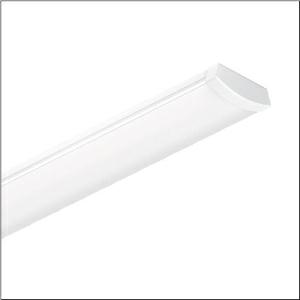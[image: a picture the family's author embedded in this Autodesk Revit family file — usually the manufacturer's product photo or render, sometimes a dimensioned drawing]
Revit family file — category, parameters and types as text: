
# Revit family: siluette_r__21_51ln12mnm70a_66ce
name_source: partatom
category: Lighting Fixtures
units: mm (PartAtom-declared; Revit-internal decimal feet)

## family parameters
Cut with Voids When Loaded = No
Host = Face
Light Source = No
Part Type = Normal
Room Calculation Point = No
Round Connector Dimension = Use Diameter
Shared = No

## types (1)
- --- (1 x LED, 4320 lm, 28.8 W, 5000K)
    Apparent Load = 29 VA
    CIE Flux Codes = 43 73 92 94 100
    Color Rendering = 80
    Color Temperature = 5000K
    Default Elevation = 1800 mm
    Description = Siluette® 21, office luminaire, primary optical cover: enclosure, of PC, frosted, light emission: direct distribution, primary light characteristic: symmetric, installation type: suspended mounting, surface-mounted, LED, rated luminous flux: 7.150lm, luminous efficacy: 140lm/W, light colour: 830/840/850, colour temperature: 3000/4000/5000K, with terminal, 3-pole, mains connection: 220..240V, AC, 50/60Hz, rated input power: 50W, housing, of sheet steel, white, length: 1.500mm, width: 152mm, height: 53mm, end cap, of PMMA, white, protection rating (complete): IP44, insulation class (complete): insulation class I (protective earthing), certification: CE, UKCA, protection symbol: D, permissible operating ambient temperature: -20..+40°C, contact your sales advisor before using the luminaires in applications with unclear chemical exposure, large temperature fluctuations or condensation-forming humidity, corresponds to IFS (International Featured Standards) requirements for safety and quality in the food industry, packaging unit: 1 piece
    Height = 52 mm  [stored 0.170604 ft]
    Lamp = 1 x LED
    Lamp Light Flux = 4320 lm
    Lamp Power = 28.8 W
    Lamp count = 1
    Length = 1485 mm
    Luminous efficacy = 150 lm/W
    Manufacturer = Siteco
    ModVariant = No
    Model = 51LN12MNM70A
    Mounting Place = Ceiling
    Mounting Type = Pendant
    Number of Poles = 1
    OnlyDefault = Yes
    Power Factor = 1
    Product Name = Siluette® 21
    Product group = office luminaire | ceiling pendant
    ProductGroupID = 902
    Protection Class = Protection class I
    Protection Degree = IP 44
    RLX_Detail_Level = 1
    RLX_Emergency_Light_Flux = 0 lm
    RLX_Emergency_Type = 0
    RLX_Emergency_Type_DB = No
    RlxData = <blob elided: 20193 chars, md5=e2df0758>
    Socket = socket
    Standby Power = 0 W
    System Light Flux = 4320 lm
    System Power = 29 W
    Type Comments = individual setting: colour temperature 5000K, luminous flux: 61 % | (OFF | OFF | ON) | 200 mA
    Type Image = l_1296910.jpg
    URL = http://relux.com
    VarID = @adj_019193
    Voltage = 0 V
    Weight = 0.00 kg
    Width = 152 mm

note: [stored X ft] marks values corroborated as IEEE doubles in the binary element streams (Revit-internal decimal feet)

## geometry (parser evidence)
native form markers: Blend x4, Sweep x11
no freeform markers — native parametric forms only
